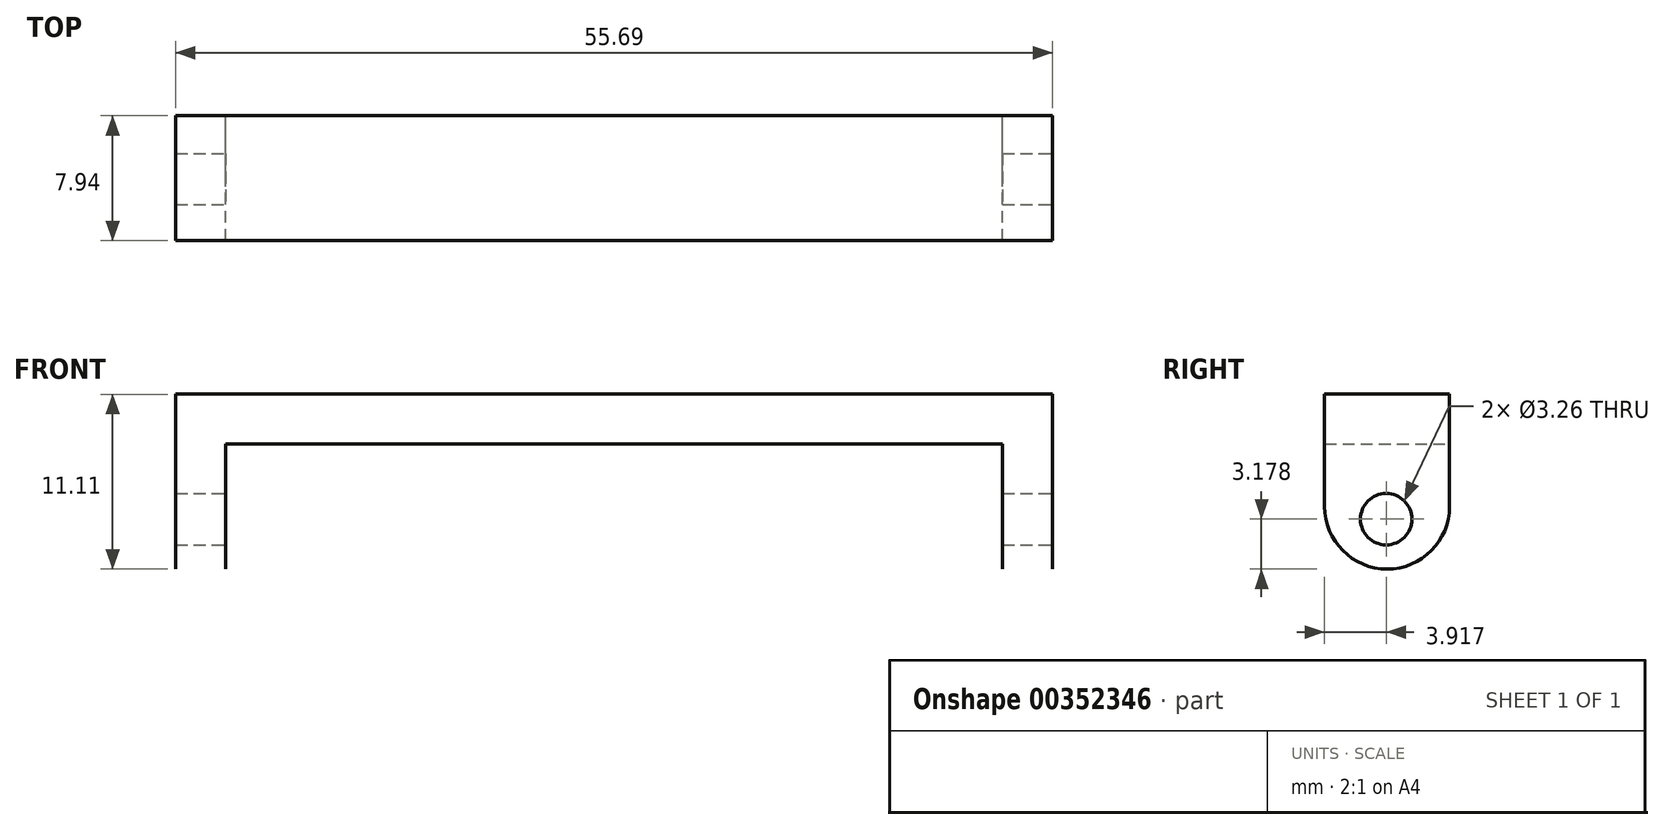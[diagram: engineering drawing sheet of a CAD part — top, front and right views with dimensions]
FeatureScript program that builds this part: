
annotation { "Feature Type Name" : "Feature", "Feature Type Description" : "" }
export const myFeature = defineFeature(function(context is Context, id is Id, definition is map)
    precondition{}
    {
        {
            var Q0;
            Q0=qCreatedBy(makeId("Top.planeOp"),FACE);
            var sketch = newSketch(context, id + "F0", { "sketchPlane" : qUnion([Q0])});
            skLineSegment(sketch, "E0.bottom", {"start": v(-29.72, 20.8) * mm, "end": v(19.5, 20.8) * mm});
            skLineSegment(sketch, "E0.top", {"start": v(-29.72, 12.85) * mm, "end": v(19.5, 12.85) * mm});
            skLineSegment(sketch, "E0.left", {"start": v(-29.72, 20.8) * mm, "end": v(-29.72, 12.85) * mm});
            skLineSegment(sketch, "E0.right", {"start": v(19.5, 20.8) * mm, "end": v(19.5, 12.85) * mm});
            skSolve(sketch);
        }
        {
            var Q0;
            Q0=makeQuery(id+"F0.imprint","IMPRINT",FACE,{"disambiguationData":[TD([[makeQuery(id+"F0.imprint","IMPRINT",EDGE,{"derivedFrom":sQuery(id+"F0.wireOp",EDGE,"E0.bottom")}),-1.0]])]});
            extrude(context, id + "F1", {"entities" : qUnion([Q0]), "depth" : 3.17 * mm});
        }
        {
            var Q0;
            Q0=makeQuery(id+"F1.opExtrude","SWEPT_FACE",FACE,{"disambiguationData":[OSD([sQuery(id+"F0.wireOp",EDGE,"E0.right")])]});
            extrude(context, id + "F2", {"entities" : qUnion([Q0]), "operationType" : NewBodyOperationType.ADD, "depth" : 3.3 * mm});
        }
        {
            var Q0;
            Q0=makeQuery(id+"F1.opExtrude","SWEPT_FACE",FACE,{"disambiguationData":[OSD([sQuery(id+"F0.wireOp",EDGE,"E0.left")])]});
            extrude(context, id + "F3", {"entities" : qUnion([Q0]), "operationType" : NewBodyOperationType.ADD, "depth" : 3.17 * mm});
        }
        {
            var Q0;
            {var subQ0=sQuery(id+"F0.wireOp",EDGE,"E0.left");var subQ1=sQuery(id+"F0.wireOp",EDGE,"E0.right");Q0=makeQuery(id+"F3.boolean.opBoolean","MERGE",FACE,{"derivedFrom":[makeQuery(id+"F2.boolean.opBoolean","MERGE",FACE,{"derivedFrom":[makeQuery(id+"F1.opExtrude","CAP_FACE",FACE,{"disambiguationData":[OSD([sQuery(id+"F0.wireOp",EDGE,"E0.bottom"),sQuery(id+"F0.wireOp",EDGE,"E0.top"),subQ0,subQ1])],"isStart":true}),makeQuery(id+"F2.opExtrude","SWEPT_FACE",FACE,{"disambiguationData":[OSD([subQ1]),TDD([makeQuery(id+"F1.opExtrude","CAP_EDGE",EDGE,{"disambiguationData":[OSD([subQ1])],"isStart":true})])]})]}),makeQuery(id+"F3.opExtrude","SWEPT_FACE",FACE,{"disambiguationData":[OSD([subQ0]),TDD([makeQuery(id+"F1.opExtrude","CAP_EDGE",EDGE,{"disambiguationData":[OSD([subQ0])],"isStart":true})])]})]});}
            var sketch = newSketch(context, id + "F4", { "sketchPlane" : qUnion([Q0])});
            skLineSegment(sketch, "E1.bottom", {"start": v(22.8, -12.85) * mm, "end": v(19.62, -12.85) * mm});
            skLineSegment(sketch, "E1.top", {"start": v(22.8, -20.8) * mm, "end": v(19.62, -20.8) * mm});
            skLineSegment(sketch, "E1.left", {"start": v(22.8, -12.85) * mm, "end": v(22.8, -20.8) * mm});
            skLineSegment(sketch, "E1.right", {"start": v(19.62, -12.85) * mm, "end": v(19.62, -20.8) * mm});
            skLineSegment(sketch, "E2.bottom", {"start": v(-32.9, -12.85) * mm, "end": v(-29.72, -12.85) * mm});
            skLineSegment(sketch, "E2.top", {"start": v(-32.9, -20.8) * mm, "end": v(-29.72, -20.8) * mm});
            skLineSegment(sketch, "E2.left", {"start": v(-32.9, -12.85) * mm, "end": v(-32.9, -20.8) * mm});
            skLineSegment(sketch, "E2.right", {"start": v(-29.72, -12.85) * mm, "end": v(-29.72, -20.8) * mm});
            skSolve(sketch);
        }
        {
            var Q0;
            Q0=makeQuery(id+"F4.imprint","IMPRINT",FACE,{"disambiguationData":[TD([[makeQuery(id+"F4.imprint","IMPRINT",EDGE,{"derivedFrom":sQuery(id+"F4.wireOp",EDGE,"E1.bottom")}),-1.0]])]});
            var Q1;
            Q1=makeQuery(id+"F4.imprint","IMPRINT",FACE,{"disambiguationData":[TD([[makeQuery(id+"F4.imprint","IMPRINT",EDGE,{"derivedFrom":sQuery(id+"F4.wireOp",EDGE,"E2.bottom")}),-1.0]])]});
            extrude(context, id + "F5", {"entities" : qUnion([Q0, Q1]), "operationType" : NewBodyOperationType.ADD, "depth" : 7.94 * mm});
        }
        {
            var Q0;
            Q0=makeQuery(id+"F5.boolean.opBoolean","MERGE",FACE,{"derivedFrom":[makeQuery(id+"F2.opExtrude","CAP_FACE",FACE,{"disambiguationData":[OSD([sQuery(id+"F0.wireOp",EDGE,"E0.right")])],"isStart":false}),makeQuery(id+"F5.opExtrude","SWEPT_FACE",FACE,{"disambiguationData":[OSD([sQuery(id+"F4.wireOp",EDGE,"E1.left")])]})]});
            var sketch = newSketch(context, id + "F6", { "sketchPlane" : qUnion([Q0])});
            skPoint(sketch, "E3", {"position": v(16.77, -4.76) * mm});
            skSolve(sketch);
        }
        {
            var Q0;
            Q0=sQuery(id+"F6.wireOp",VERTEX,"E3");
            var Q1;
            Q1=makeQuery(id+"F1.opExtrude","SWEPT_BODY",BODY,{"disambiguationData":[OSD([sQuery(id+"F0.wireOp",EDGE,"E0.bottom"),sQuery(id+"F0.wireOp",EDGE,"E0.top"),sQuery(id+"F0.wireOp",EDGE,"E0.left"),sQuery(id+"F0.wireOp",EDGE,"E0.right")])]});
            hole(context, id + "F7", {"style" : HoleStyle.SIMPLE, "endStyle" : HoleEndStyle.THROUGH, "standardTappedOrClearance" : lookupTablePath({ "standard" : "ANSI", "fit" : "Normal (ASME)", "size" : "#4", "type" : "Clearance" }), "standardBlindInLast" : lookupTablePath({ "fit" : "Free", "standard" : "ANSI", "size" : "#4", "type" : "Clearance" }), "holeDiameter" : 3.26 * mm, "isTappedThrough" : true, "tappedDepth" : 12.7 * mm, "tapClearance" : 3, "locations" : qUnion([Q0]), "scope" : qUnion([Q1])});
        }
        {
            var Q0;
            Q0=makeQuery(id+"F5.opExtrude","CAP_EDGE",EDGE,{"disambiguationData":[OSD([sQuery(id+"F4.wireOp",EDGE,"E1.bottom")])],"isStart":false});
            var Q1;
            Q1=makeQuery(id+"F5.opExtrude","CAP_EDGE",EDGE,{"disambiguationData":[OSD([sQuery(id+"F4.wireOp",EDGE,"E1.top")])],"isStart":false});
            var Q2;
            Q2=makeQuery(id+"F5.opExtrude","CAP_EDGE",EDGE,{"disambiguationData":[OSD([sQuery(id+"F4.wireOp",EDGE,"E2.bottom")])],"isStart":false});
            var Q3;
            Q3=makeQuery(id+"F5.opExtrude","CAP_EDGE",EDGE,{"disambiguationData":[OSD([sQuery(id+"F4.wireOp",EDGE,"E2.top")])],"isStart":false});
            fillet(context, id + "F8", {"entities" : qUnion([Q0, Q1, Q2, Q3]), "radius" : 4 * mm, "tangentPropagation" : true, "allowEdgeOverflow" : false});
        }
    });
